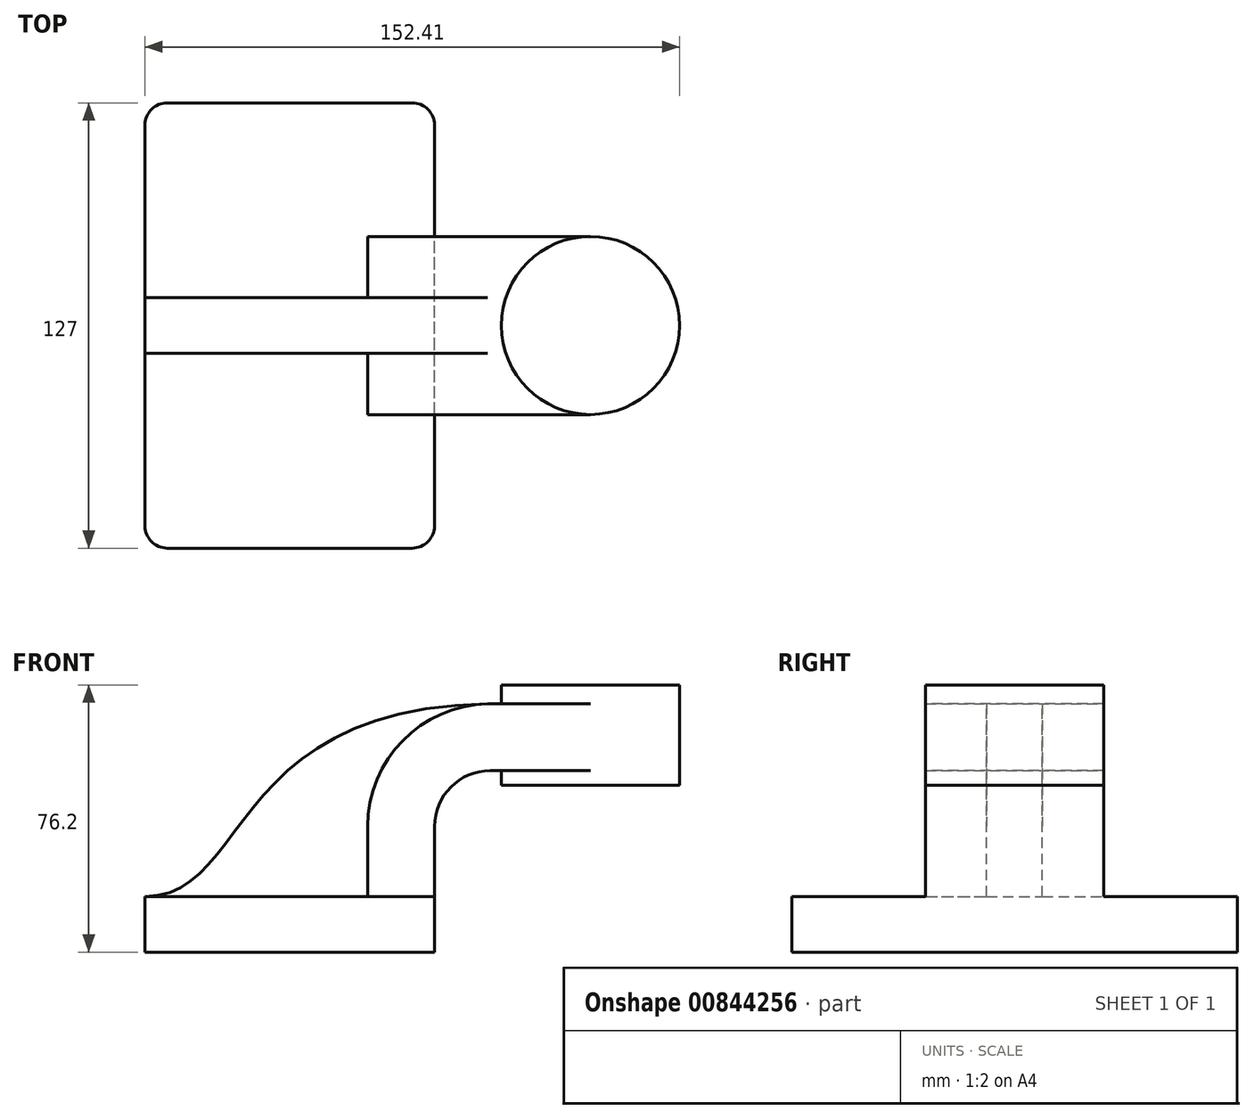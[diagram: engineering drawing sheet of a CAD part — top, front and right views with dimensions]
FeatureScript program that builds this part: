
annotation { "Feature Type Name" : "Feature", "Feature Type Description" : "" }
export const myFeature = defineFeature(function(context is Context, id is Id, definition is map)
    precondition{}
    {
        {
            var Q0;
            Q0=qCreatedBy(makeId("Front.planeOp"),FACE);
            var sketch = newSketch(context, id + "F0", { "sketchPlane" : qUnion([Q0])});
            skLineSegment(sketch, "E0.bottom", {"start": v(41.28, -7.94) * mm, "end": v(-41.28, -7.94) * mm});
            skLineSegment(sketch, "E0.top", {"start": v(41.28, 7.94) * mm, "end": v(-41.28, 7.94) * mm});
            skLineSegment(sketch, "E0.left", {"start": v(41.28, -7.94) * mm, "end": v(41.28, 7.94) * mm});
            skLineSegment(sketch, "E0.right", {"start": v(-41.28, -7.94) * mm, "end": v(-41.28, 7.94) * mm});
            skPoint(sketch, "E0.middle", {"position": v(0, 0) * mm});
            skLineSegment(sketch, "E1.bottom", {"start": v(60.33, 39.69) * mm, "end": v(111.12, 39.69) * mm});
            skLineSegment(sketch, "E1.top", {"start": v(60.32, 68.26) * mm, "end": v(111.12, 68.26) * mm});
            skLineSegment(sketch, "E1.left", {"start": v(60.33, 39.69) * mm, "end": v(60.32, 68.26) * mm});
            skLineSegment(sketch, "E1.right", {"start": v(111.12, 39.69) * mm, "end": v(111.12, 68.26) * mm});
            skPoint(sketch, "E1.middle", {"position": v(85.72, 53.98) * mm});
            skLineSegment(sketch, "E2", {"start": v(41.28, 7.94) * mm, "end": v(41.28, 27.9) * mm});
            skArc(sketch, "E3", {"start": v(41.28, 27.9) * mm, "mid": v(45.92, 39.13) * mm, "end": v(57.15, 43.78) * mm});
            skLineSegment(sketch, "E4", {"start": v(57.15, 43.78) * mm, "end": v(85.72, 43.78) * mm});
            skLineSegment(sketch, "E5.0", {"start": v(57.15, 62.83) * mm, "end": v(85.72, 62.83) * mm});
            skArc(sketch, "E5.1", {"start": v(22.23, 27.9) * mm, "mid": v(32.45, 52.6) * mm, "end": v(57.15, 62.83) * mm});
            skLineSegment(sketch, "E5.2", {"start": v(22.23, 7.94) * mm, "end": v(22.23, 27.9) * mm});
            skLineSegment(sketch, "E6", {"start": v(85.72, 62.83) * mm, "end": v(85.72, 43.78) * mm});
            skLineSegment(sketch, "E7", {"start": v(85.72, 62.83) * mm, "end": v(85.72, 68.26) * mm});
            skLineSegment(sketch, "E8", {"start": v(85.72, 43.78) * mm, "end": v(85.72, 39.69) * mm});
            skFitSpline(sketch, "E9", {"points": [v(-41.28, 7.94) * mm, v(57.15, 62.83) * mm], "startDerivative": vector(89.84, 0) * mm, "endDerivative": vector(224.38, 1.83) * mm});
            skSolve(sketch);
        }
        {
            var Q0;
            Q0=makeQuery(id+"F0.imprint","IMPRINT",FACE,{"disambiguationData":[TD([[makeQuery(id+"F0.imprint","IMPRINT",EDGE,{"derivedFrom":sQuery(id+"F0.wireOp",EDGE,"E0.bottom")}),-1.0]])]});
            extrude(context, id + "F1", {"entities" : qUnion([Q0]), "endBound" : BoundingType.SYMMETRIC, "depth" : 127 * mm, "offsetDistance" : 25.4 * mm});
        }
        {
            var Q0;
            {var subQ1=sQuery(id+"F0.wireOp",EDGE,"E2");Q0=makeQuery(id+"F0.imprint","IMPRINT",FACE,{"disambiguationData":[TD([[makeQuery(id+"F0.imprint","IMPRINT",EDGE,{"derivedFrom":subQ1}),1.0]])]});}
            var Q1;
            {var subQ5=sQuery(id+"F0.wireOp",EDGE,"E6");Q1=makeQuery(id+"F0.imprint","IMPRINT",FACE,{"disambiguationData":[TD([[makeQuery(id+"F0.imprint","IMPRINT",EDGE,{"derivedFrom":subQ5}),-1.0]])]});}
            extrude(context, id + "F2", {"entities" : qUnion([Q0, Q1]), "operationType" : NewBodyOperationType.ADD, "endBound" : BoundingType.SYMMETRIC, "depth" : 50.8 * mm, "offsetDistance" : 25.4 * mm});
        }
        {
            var Q0;
            {var subQ3=sQuery(id+"F0.wireOp",EDGE,"E5.2");Q0=makeQuery(id+"F0.imprint","IMPRINT",FACE,{"disambiguationData":[TD([[makeQuery(id+"F0.imprint","IMPRINT",EDGE,{"derivedFrom":subQ3}),1.0]])]});}
            extrude(context, id + "F3", {"entities" : qUnion([Q0]), "operationType" : NewBodyOperationType.ADD, "endBound" : BoundingType.SYMMETRIC, "depth" : 15.88 * mm, "offsetDistance" : 25.4 * mm});
        }
        {
            var Q0;
            {var subQ0=sQuery(id+"F0.wireOp",EDGE,"E1.right");Q0=makeQuery(id+"F0.imprint","IMPRINT",FACE,{"disambiguationData":[TD([[makeQuery(id+"F0.imprint","IMPRINT",EDGE,{"derivedFrom":subQ0}),1.0]])]});}
            var Q1;
            Q1=sQuery(id+"F0.wireOp",EDGE,"E6");
            revolve(context, id + "F4", {"operationType" : NewBodyOperationType.ADD, "surfaceOperationType" : NewSurfaceOperationType.NEW, "entities" : qUnion([Q0]), "axis" : qUnion([Q1]), "revolveType" : RevolveType.FULL});
        }
        {
            var Q0;
            Q0=makeQuery(id+"F1.opExtrude","CAP_EDGE",EDGE,{"disambiguationData":[OSD([sQuery(id+"F0.wireOp",EDGE,"E0.right")])],"isStart":false});
            var Q1;
            Q1=makeQuery(id+"F1.opExtrude","CAP_EDGE",EDGE,{"disambiguationData":[OSD([sQuery(id+"F0.wireOp",EDGE,"E0.left")])],"isStart":false});
            var Q2;
            Q2=makeQuery(id+"F1.opExtrude","CAP_EDGE",EDGE,{"disambiguationData":[OSD([sQuery(id+"F0.wireOp",EDGE,"E0.left")])],"isStart":true});
            var Q3;
            Q3=makeQuery(id+"F1.opExtrude","CAP_EDGE",EDGE,{"disambiguationData":[OSD([sQuery(id+"F0.wireOp",EDGE,"E0.right")])],"isStart":true});
            fillet(context, id + "F5", {"entities" : qUnion([Q0, Q1, Q2, Q3]), "radius" : 6.35 * mm, "tangentPropagation" : true, "allowEdgeOverflow" : false});
        }
    });
